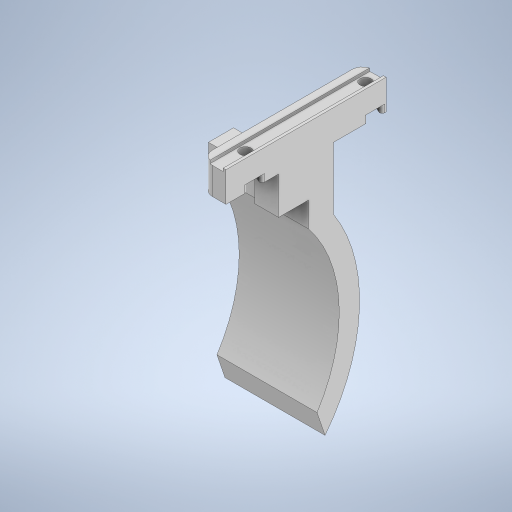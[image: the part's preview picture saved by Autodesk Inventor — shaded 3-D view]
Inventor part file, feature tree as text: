
AUTODESK INVENTOR PART (.ipt)
format: ipt  version: 2024 (Build 280153000, 153)  size: 336,896 bytes
history: native  units: in
note: dims shown in document units (in); Inventor stores cm internally (conversion verified against a paired STEP export)
features: sketch x7, extrude x5, projected_geometry x4, fillet x2, sweep x1
ambient origin geometry x8: Origin, YZ Plane, XZ Plane, XY Plane, X Axis, Y Axis, Z Axis, Center Point
bodies: Solid1 (feature_tree)
feature tree (19):
  extrude  "Extrusion1"  Depth=2.5197in
  extrude  "Extrusion2"  Depth=1.8898in
  extrude  "Extrusion3"  Depth=0.4724in TaperAngle=0.0deg
  fillet  "Fillet1"  Radius=0.0433in
  fillet  "Fillet2"  Radius=0.2126in
  extrude  "Extrusion15"  Depth=0.4724in TaperAngle=0.0deg
  extrude  "Extrusion16"  Depth=0.1181in TaperAngle=0.0deg
  sweep  "Sweep1"
  sketch  "Sketch1"  dims[d1=0.374in d2=2.5197in]
  sketch  "Sketch2"  dims[d3=0.1772in d4=1.8898in]
  sketch  "Sketch3"  dims[d6=0.1457in d7=0.4724in d8=0.0in d9=0.0433in d10=0.2126in]
  projected_geometry  "Projected Loop2"
  projected_geometry  "Projected Loop3"
  projected_geometry  "Projected Loop4"
  projected_geometry  "Projected Loop5"
  sketch  "Sketch15"  dims[d11=0.0472in d12=0.4724in d13=0.0in]
  sketch  "Sketch16"  dims[d14=0.2953in d15=0.1181in d16=0.0in]
  sketch  "Sketch17"  dims[d17=0.1772in d18=0.0394in]
  sketch  "Sketch18"  dims[d19=0.1575in d76=0.4724in d79=0.4331in d80=0.8661in d81=0.5906in d82=0.0in d83=1.5748in d84=0.3937in d85=0.3937in d86=0.0in d87=2.7559in d88=2.3622in d89=0.0in d90=0.0in d42=0.0197in d43=0.0344in d44=0.0197in d45=0.0344in d46=0.0in d47=0.0in d48=0.0in d49=0.0in d50=0.0in d51=0.0in d52=0.0in d53=0.0in d55=0.0197in d56=0.0344in d57=0.0197in d58=0.0344in d60=0.0197in d61=0.0344in d62=0.0197in d63=0.0344in d72=0.0197in d73=0.0344in d74=0.0197in d75=0.0344in]
